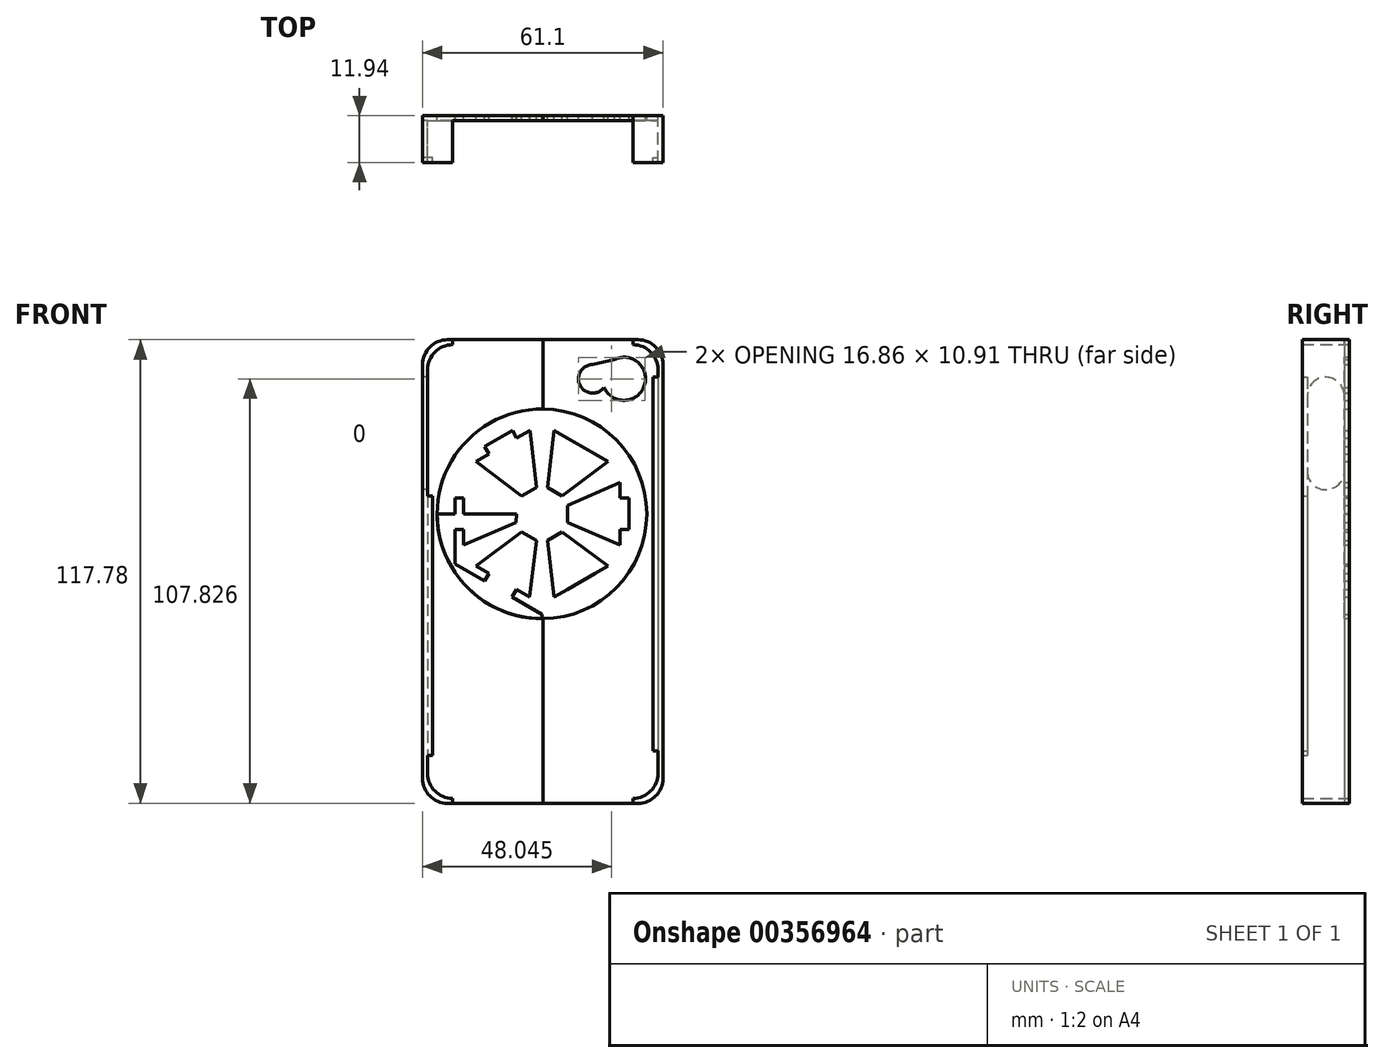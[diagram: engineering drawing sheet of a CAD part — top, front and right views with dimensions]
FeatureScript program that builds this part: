
annotation { "Feature Type Name" : "Feature", "Feature Type Description" : "" }
export const myFeature = defineFeature(function(context is Context, id is Id, definition is map)
    precondition{}
    {
        {
            var Q0;
            Q0=qCreatedBy(makeId("Front.planeOp"),FACE);
            var sketch = newSketch(context, id + "F0", { "sketchPlane" : qUnion([Q0])});
            skLineSegment(sketch, "E0.left", {"start": v(-75.12, 56.4) * mm, "end": v(-75.12, -46.14) * mm});
            skLineSegment(sketch, "E0.right", {"start": v(-16.58, 56.4) * mm, "end": v(-16.58, -46.14) * mm});
            skPoint(sketch, "E1.visualSharp", {"position": v(-16.58, 62.75) * mm});
            skArc(sketch, "E1.filletArc", {"start": v(-16.58, 56.4) * mm, "mid": v(-18.43, 60.88) * mm, "end": v(-22.9, 62.75) * mm});
            skPoint(sketch, "E2.visualSharp", {"position": v(-75.12, 62.75) * mm});
            skArc(sketch, "E2.filletArc", {"start": v(-68.77, 62.75) * mm, "mid": v(-73.26, 60.89) * mm, "end": v(-75.12, 56.4) * mm});
            skPoint(sketch, "E3.visualSharp", {"position": v(-75.12, -52.5) * mm});
            skArc(sketch, "E3.filletArc", {"start": v(-75.12, -46.14) * mm, "mid": v(-73.26, -50.63) * mm, "end": v(-68.77, -52.5) * mm});
            skPoint(sketch, "E4.visualSharp", {"position": v(-16.58, -52.5) * mm});
            skArc(sketch, "E4.filletArc", {"start": v(-22.93, -52.5) * mm, "mid": v(-18.44, -50.63) * mm, "end": v(-16.58, -46.14) * mm});
            skLineSegment(sketch, "E5.bottom", {"start": v(-70.04, 64.02) * mm, "end": v(-68.77, 64.02) * mm});
            skLineSegment(sketch, "E5.top", {"start": v(-70.04, -53.76) * mm, "end": v(-68.77, -53.76) * mm});
            skLineSegment(sketch, "E5.left", {"start": v(-76.4, 57.67) * mm, "end": v(-76.4, -47.41) * mm});
            skLineSegment(sketch, "E5.right", {"start": v(-15.3, 57.67) * mm, "end": v(-15.3, -47.41) * mm});
            skPoint(sketch, "E6.visualSharp", {"position": v(-15.3, 64.02) * mm});
            skArc(sketch, "E6.filletArc", {"start": v(-15.3, 57.67) * mm, "mid": v(-17.17, 62.16) * mm, "end": v(-21.66, 64.02) * mm});
            skPoint(sketch, "E7.visualSharp", {"position": v(-76.4, 64.02) * mm});
            skArc(sketch, "E7.filletArc", {"start": v(-70.04, 64.02) * mm, "mid": v(-74.53, 62.16) * mm, "end": v(-76.4, 57.67) * mm});
            skPoint(sketch, "E8.visualSharp", {"position": v(-76.4, -53.76) * mm});
            skArc(sketch, "E8.filletArc", {"start": v(-76.4, -47.41) * mm, "mid": v(-74.53, -51.9) * mm, "end": v(-70.04, -53.76) * mm});
            skPoint(sketch, "E9.visualSharp", {"position": v(-15.3, -53.76) * mm});
            skArc(sketch, "E9.filletArc", {"start": v(-21.66, -53.76) * mm, "mid": v(-17.17, -51.9) * mm, "end": v(-15.3, -47.41) * mm});
            skLineSegment(sketch, "E10", {"start": v(-68.77, -52.5) * mm, "end": v(-68.77, -53.76) * mm});
            skLineSegment(sketch, "E11", {"start": v(-22.93, -52.5) * mm, "end": v(-22.93, -53.76) * mm});
            skLineSegment(sketch, "E12.trimOffspring", {"start": v(-22.93, -53.76) * mm, "end": v(-21.66, -53.76) * mm});
            skLineSegment(sketch, "E13", {"start": v(-68.77, 62.75) * mm, "end": v(-68.77, 64.02) * mm});
            skLineSegment(sketch, "E14", {"start": v(-22.9, 62.75) * mm, "end": v(-22.9, 64.02) * mm});
            skLineSegment(sketch, "E15.trimOffspring", {"start": v(-22.9, 64.02) * mm, "end": v(-21.66, 64.02) * mm});
            skLineSegment(sketch, "E16", {"start": v(-68.77, 64.02) * mm, "end": v(-22.9, 64.02) * mm});
            skLineSegment(sketch, "E17", {"start": v(-68.77, -53.76) * mm, "end": v(-22.93, -53.76) * mm});
            skCircle(sketch, "E18", {"center": v(-25.24, 54.09) * mm, "radius": 5.48 * mm});
            skCircle(sketch, "E19", {"center": v(-33.16, 54.09) * mm, "radius": 3.63 * mm});
            skLineSegment(sketch, "E20", {"start": v(-25.24, 59.57) * mm, "end": v(-33.16, 57.72) * mm});
            skLineSegment(sketch, "E21", {"start": v(-26.52, 48.75) * mm, "end": v(-34.01, 50.56) * mm});
            skLineSegment(sketch, "E22", {"start": v(-45.84, 64.02) * mm, "end": v(-45.84, -53.76) * mm});
            skCircle(sketch, "E23", {"center": v(-46.06, 19.78) * mm, "radius": 26.63 * mm});
            skLineSegment(sketch, "E24", {"start": v(-46.06, 46.4) * mm, "end": v(-46.06, -6.85) * mm});
            skLineSegment(sketch, "E25.5", {"start": v(-46.06, 45.29) * mm, "end": v(-23.97, 32.53) * mm});
            skPoint(sketch, "E25.0.midPoint", {"position": v(-23.97, 19.78) * mm});
            skPoint(sketch, "E26.0.midPoint", {"position": v(-36.14, 37) * mm});
            skPoint(sketch, "E27.0.midPoint", {"position": v(-39.54, 19.78) * mm});
            skLineSegment(sketch, "E28", {"start": v(-44.67, 26.5) * mm, "end": v(-42.99, 40.94) * mm});
            skLineSegment(sketch, "E29", {"start": v(-38.53, 40.94) * mm, "end": v(-39.64, 39.01) * mm});
            skLineSegment(sketch, "E30", {"start": v(-42.99, 40.94) * mm, "end": v(-46.08, 42.72) * mm});
            skLineSegment(sketch, "E31", {"start": v(-40.93, 24.35) * mm, "end": v(-29.3, 33.05) * mm});
            skLineSegment(sketch, "E32", {"start": v(-32.64, 34.98) * mm, "end": v(-31.53, 36.9) * mm});
            skLineSegment(sketch, "E33", {"start": v(-26.2, 27.7) * mm, "end": v(-39.54, 21.94) * mm});
            skLineSegment(sketch, "E34", {"start": v(-26.2, 23.84) * mm, "end": v(-23.97, 23.84) * mm});
            skLineSegment(sketch, "E35", {"start": v(-46.06, 19.78) * mm, "end": v(-19.44, 19.8) * mm});
            skLineSegment(sketch, "E36", {"start": v(-23.97, 32.53) * mm, "end": v(-23.97, 19.78) * mm});
            skLineSegment(sketch, "E37", {"start": v(-26.2, 31.27) * mm, "end": v(-29.3, 33.05) * mm});
            skLineSegment(sketch, "E38", {"start": v(-29.3, 33.05) * mm, "end": v(-32.64, 34.98) * mm});
            skLineSegment(sketch, "E39", {"start": v(-32.64, 34.98) * mm, "end": v(-39.64, 39.01) * mm});
            skLineSegment(sketch, "E40", {"start": v(-39.64, 39.01) * mm, "end": v(-42.99, 40.94) * mm});
            skLineSegment(sketch, "E41", {"start": v(-26.2, 31.27) * mm, "end": v(-26.2, 27.7) * mm});
            skLineSegment(sketch, "E42", {"start": v(-26.2, 27.7) * mm, "end": v(-26.2, 23.84) * mm});
            skLineSegment(sketch, "E43", {"start": v(-26.2, 23.84) * mm, "end": v(-26.2, 19.8) * mm});
            skPoint(sketch, "E44", {"position": v(-46.06, 27.3) * mm});
            skLineSegment(sketch, "E45", {"start": v(-46.06, 27.3) * mm, "end": v(-44.67, 26.5) * mm});
            skLineSegment(sketch, "E46", {"start": v(-44.67, 26.5) * mm, "end": v(-40.93, 24.35) * mm});
            skLineSegment(sketch, "E47", {"start": v(-40.93, 24.35) * mm, "end": v(-39.54, 23.54) * mm});
            skLineSegment(sketch, "E48", {"start": v(-39.54, 23.54) * mm, "end": v(-39.54, 21.94) * mm});
            skLineSegment(sketch, "E49", {"start": v(-39.54, 21.94) * mm, "end": v(-39.54, 19.78) * mm});
            skLineSegment(sketch, "E50.MirrorCS", {"start": v(-46.02, -5.73) * mm, "end": v(-23.95, 7.06) * mm});
            skLineSegment(sketch, "E51.MirrorCS", {"start": v(-23.95, 7.06) * mm, "end": v(-23.97, 19.81) * mm});
            skLineSegment(sketch, "E52.MirrorCS", {"start": v(-42.95, -1.38) * mm, "end": v(-46.05, -3.16) * mm});
            skLineSegment(sketch, "E53.MirrorCS", {"start": v(-39.61, 0.56) * mm, "end": v(-42.95, -1.38) * mm});
            skLineSegment(sketch, "E54.MirrorCS", {"start": v(-38.5, -1.37) * mm, "end": v(-39.61, 0.56) * mm});
            skLineSegment(sketch, "E55.MirrorCS", {"start": v(-32.62, 4.6) * mm, "end": v(-39.61, 0.56) * mm});
            skLineSegment(sketch, "E56.MirrorCS", {"start": v(-32.62, 4.6) * mm, "end": v(-31.5, 2.68) * mm});
            skLineSegment(sketch, "E57.MirrorCS", {"start": v(-29.28, 6.54) * mm, "end": v(-32.62, 4.6) * mm});
            skLineSegment(sketch, "E58.MirrorCS", {"start": v(-26.19, 8.32) * mm, "end": v(-29.28, 6.54) * mm});
            skLineSegment(sketch, "E59.MirrorCS", {"start": v(-26.19, 8.32) * mm, "end": v(-26.19, 11.9) * mm});
            skLineSegment(sketch, "E60.MirrorCS", {"start": v(-26.19, 11.9) * mm, "end": v(-26.2, 15.76) * mm});
            skLineSegment(sketch, "E61.MirrorCS", {"start": v(-26.2, 15.76) * mm, "end": v(-26.2, 19.8) * mm});
            skLineSegment(sketch, "E62.MirrorCS", {"start": v(-26.19, 11.9) * mm, "end": v(-39.54, 17.63) * mm});
            skLineSegment(sketch, "E63.MirrorCS", {"start": v(-40.93, 15.22) * mm, "end": v(-29.28, 6.54) * mm});
            skLineSegment(sketch, "E64.MirrorCS", {"start": v(-44.66, 13.06) * mm, "end": v(-42.95, -1.38) * mm});
            skLineSegment(sketch, "E65.MirrorCS", {"start": v(-44.66, 13.06) * mm, "end": v(-40.93, 15.22) * mm});
            skPoint(sketch, "E66.MirrorP", {"position": v(-46.05, 12.25) * mm});
            skLineSegment(sketch, "E67.MirrorCS", {"start": v(-46.05, 12.25) * mm, "end": v(-44.66, 13.06) * mm});
            skLineSegment(sketch, "E68.MirrorCS", {"start": v(-40.93, 15.22) * mm, "end": v(-39.54, 16.03) * mm});
            skLineSegment(sketch, "E69.MirrorCS", {"start": v(-39.54, 16.03) * mm, "end": v(-39.54, 17.63) * mm});
            skLineSegment(sketch, "E70.MirrorCS", {"start": v(-39.54, 17.63) * mm, "end": v(-39.54, 19.79) * mm});
            skLineSegment(sketch, "E71.MirrorCS", {"start": v(-52.59, 16.03) * mm, "end": v(-52.59, 17.63) * mm});
            skLineSegment(sketch, "E72.MirrorCS", {"start": v(-51.2, 15.22) * mm, "end": v(-52.59, 16.03) * mm});
            skLineSegment(sketch, "E73.MirrorCS", {"start": v(-52.58, 21.94) * mm, "end": v(-52.58, 19.78) * mm});
            skLineSegment(sketch, "E74.MirrorCS", {"start": v(-51.2, 24.35) * mm, "end": v(-52.58, 23.54) * mm});
            skLineSegment(sketch, "E75.MirrorCS", {"start": v(-52.59, 17.63) * mm, "end": v(-52.58, 19.79) * mm});
            skLineSegment(sketch, "E76.MirrorCS", {"start": v(-52.58, 23.54) * mm, "end": v(-52.58, 21.94) * mm});
            skLineSegment(sketch, "E77.MirrorCS", {"start": v(-65.93, 23.84) * mm, "end": v(-68.16, 23.84) * mm});
            skLineSegment(sketch, "E78.MirrorCS", {"start": v(-53.63, -1.37) * mm, "end": v(-52.52, 0.56) * mm});
            skLineSegment(sketch, "E79.MirrorCS", {"start": v(-59.49, 34.98) * mm, "end": v(-60.6, 36.9) * mm});
            skLineSegment(sketch, "E80.MirrorCS", {"start": v(-59.5, 4.6) * mm, "end": v(-60.62, 2.68) * mm});
            skLineSegment(sketch, "E81.MirrorCS", {"start": v(-53.6, 40.94) * mm, "end": v(-52.48, 39.01) * mm});
            skLineSegment(sketch, "E82.MirrorCS", {"start": v(-65.94, 11.9) * mm, "end": v(-65.94, 15.76) * mm});
            skPoint(sketch, "E83.MirrorP", {"position": v(-52.58, 19.78) * mm});
            skLineSegment(sketch, "E84.MirrorCS", {"start": v(-65.93, 23.84) * mm, "end": v(-65.93, 19.8) * mm});
            skLineSegment(sketch, "E85.MirrorCS", {"start": v(-49.17, -1.38) * mm, "end": v(-46.08, -3.16) * mm});
            skLineSegment(sketch, "E86.MirrorCS", {"start": v(-62.85, 6.54) * mm, "end": v(-59.5, 4.6) * mm});
            skLineSegment(sketch, "E87.MirrorCS", {"start": v(-47.47, 13.06) * mm, "end": v(-49.17, -1.38) * mm});
            skLineSegment(sketch, "E88.MirrorCS", {"start": v(-68.18, 7.06) * mm, "end": v(-68.15, 19.81) * mm});
            skLineSegment(sketch, "E89.MirrorCS", {"start": v(-62.83, 33.05) * mm, "end": v(-59.49, 34.98) * mm});
            skLineSegment(sketch, "E90.MirrorCS", {"start": v(-65.94, 15.76) * mm, "end": v(-65.93, 19.8) * mm});
            skLineSegment(sketch, "E91.MirrorCS", {"start": v(-59.49, 34.98) * mm, "end": v(-52.48, 39.01) * mm});
            skLineSegment(sketch, "E92.MirrorCS", {"start": v(-52.48, 39.01) * mm, "end": v(-49.14, 40.94) * mm});
            skLineSegment(sketch, "E93.MirrorCS", {"start": v(-65.94, 8.32) * mm, "end": v(-65.94, 11.9) * mm});
            skPoint(sketch, "E94.MirrorP", {"position": v(-55.98, 37) * mm});
            skLineSegment(sketch, "E95.MirrorCS", {"start": v(-65.93, 27.7) * mm, "end": v(-65.93, 23.84) * mm});
            skLineSegment(sketch, "E96.MirrorCS", {"start": v(-65.93, 27.7) * mm, "end": v(-52.58, 21.94) * mm});
            skLineSegment(sketch, "E97.MirrorCS", {"start": v(-46.06, 19.78) * mm, "end": v(-72.69, 19.8) * mm});
            skLineSegment(sketch, "E98.MirrorCS", {"start": v(-51.2, 24.35) * mm, "end": v(-62.83, 33.05) * mm});
            skPoint(sketch, "E99.MirrorP", {"position": v(-46.08, 12.25) * mm});
            skLineSegment(sketch, "E100.MirrorCS", {"start": v(-51.2, 15.22) * mm, "end": v(-62.85, 6.54) * mm});
            skLineSegment(sketch, "E101.MirrorCS", {"start": v(-47.47, 13.06) * mm, "end": v(-51.2, 15.22) * mm});
            skLineSegment(sketch, "E102.MirrorCS", {"start": v(-47.45, 26.5) * mm, "end": v(-49.14, 40.94) * mm});
            skLineSegment(sketch, "E103.MirrorCS", {"start": v(-65.94, 8.32) * mm, "end": v(-62.85, 6.54) * mm});
            skLineSegment(sketch, "E104.MirrorCS", {"start": v(-46.06, 45.29) * mm, "end": v(-68.15, 32.53) * mm});
            skLineSegment(sketch, "E105.MirrorCS", {"start": v(-68.15, 32.53) * mm, "end": v(-68.15, 19.78) * mm});
            skLineSegment(sketch, "E106.MirrorCS", {"start": v(-52.52, 0.56) * mm, "end": v(-49.17, -1.38) * mm});
            skLineSegment(sketch, "E107.MirrorCS", {"start": v(-49.14, 40.94) * mm, "end": v(-46.05, 42.72) * mm});
            skPoint(sketch, "E108.MirrorP", {"position": v(-68.15, 19.78) * mm});
            skLineSegment(sketch, "E109.MirrorCS", {"start": v(-65.92, 31.27) * mm, "end": v(-65.93, 27.7) * mm});
            skLineSegment(sketch, "E110.MirrorCS", {"start": v(-47.45, 26.5) * mm, "end": v(-51.2, 24.35) * mm});
            skLineSegment(sketch, "E111.MirrorCS", {"start": v(-59.5, 4.6) * mm, "end": v(-52.52, 0.56) * mm});
            skLineSegment(sketch, "E112.MirrorCS", {"start": v(-65.94, 11.9) * mm, "end": v(-52.59, 17.63) * mm});
            skLineSegment(sketch, "E113.MirrorCS", {"start": v(-46.1, -5.73) * mm, "end": v(-68.18, 7.06) * mm});
            skLineSegment(sketch, "E114.MirrorCS", {"start": v(-65.92, 31.27) * mm, "end": v(-62.83, 33.05) * mm});
            skLineSegment(sketch, "E115.MirrorCS", {"start": v(-46.06, 27.3) * mm, "end": v(-47.45, 26.5) * mm});
            skLineSegment(sketch, "E116.MirrorCS", {"start": v(-46.08, 12.25) * mm, "end": v(-47.47, 13.06) * mm});
            skLineSegment(sketch, "E117.MirrorCS", {"start": v(-26.2, 15.76) * mm, "end": v(-23.96, 15.76) * mm});
            skLineSegment(sketch, "E118.MirrorCS", {"start": v(-65.94, 15.76) * mm, "end": v(-68.16, 15.76) * mm});
            skLineSegment(sketch, "E119", {"start": v(-46.1, -5.73) * mm, "end": v(-46.06, -5.75) * mm});
            skLineSegment(sketch, "E120", {"start": v(-46.06, -5.75) * mm, "end": v(-46.02, -5.73) * mm});
            skLineSegment(sketch, "E121", {"start": v(-46.08, 12.25) * mm, "end": v(-46.06, 12.24) * mm});
            skLineSegment(sketch, "E122", {"start": v(-46.06, 12.24) * mm, "end": v(-46.05, 12.25) * mm});
            skSolve(sketch);
        }
        {
            var Q0;
            Q0=makeQuery(id+"F0.imprint","IMPRINT",FACE,{"disambiguationData":[TD([[makeQuery(id+"F0.imprint","IMPRINT",EDGE,{"derivedFrom":sQuery(id+"F0.wireOp",EDGE,"E0.left")}),1.0]])]});
            extrude(context, id + "F1", {"entities" : qUnion([Q0]), "depth" : 1.27 * mm});
        }
        {
            var Q0;
            Q0=makeQuery(id+"F0.imprint","IMPRINT",FACE,{"disambiguationData":[TD([[makeQuery(id+"F0.imprint","IMPRINT",EDGE,{"derivedFrom":sQuery(id+"F0.wireOp",EDGE,"E0.left")}),-1.0]])]});
            var Q1;
            Q1=makeQuery(id+"F0.imprint","IMPRINT",FACE,{"disambiguationData":[TD([[makeQuery(id+"F0.imprint","IMPRINT",EDGE,{"derivedFrom":sQuery(id+"F0.wireOp",EDGE,"E0.right")}),1.0]])]});
            extrude(context, id + "F2", {"entities" : qUnion([Q0, Q1]), "operationType" : NewBodyOperationType.ADD, "depth" : 11.94 * mm});
        }
        {
            var Q0;
            Q0=makeQuery(id+"F2.opExtrude","SWEPT_FACE",FACE,{"disambiguationData":[OSD([sQuery(id+"F0.wireOp",EDGE,"E5.left")])]});
            var sketch = newSketch(context, id + "F3", { "sketchPlane" : qUnion([Q0])});
            skCircle(sketch, "E123", {"center": v(5.97, 49.8) * mm, "radius": 4.7 * mm});
            skCircle(sketch, "E124", {"center": v(5.97, 30.62) * mm, "radius": 4.7 * mm});
            skLineSegment(sketch, "E125", {"start": v(1.27, 49.8) * mm, "end": v(1.27, 30.62) * mm});
            skLineSegment(sketch, "E126", {"start": v(10.67, 30.62) * mm, "end": v(10.67, 49.8) * mm});
            skSolve(sketch);
        }
        {
            var Q0;
            {var subQ0=sQuery(id+"F3.wireOp",EDGE,"E125");Q0=makeQuery(id+"F3.imprint","IMPRINT",FACE,{"disambiguationData":[TD([[makeQuery(id+"F3.imprint","IMPRINT",EDGE,{"derivedFrom":subQ0}),1.0]])]});}
            var Q1;
            {var subQ0=sQuery(id+"F3.wireOp",EDGE,"E123");var subQ1=makeQuery(id+"F3.imprint","INTERSECT",VERTEX,{"derivedFrom":[subQ0,sQuery(id+"F3.wireOp",EDGE,"E125")]});Q1=makeQuery(id+"F3.imprint","IMPRINT",FACE,{"disambiguationData":[TD([[makeQuery(id+"F3.imprint","IMPRINT",EDGE,{"disambiguationData":[TD([[subQ1,1.0]])],"derivedFrom":subQ0}),1.0]])]});}
            var Q2;
            {var subQ0=sQuery(id+"F3.wireOp",EDGE,"E124");var subQ1=makeQuery(id+"F3.imprint","INTERSECT",VERTEX,{"derivedFrom":[subQ0,sQuery(id+"F3.wireOp",EDGE,"E125")]});Q2=makeQuery(id+"F3.imprint","IMPRINT",FACE,{"disambiguationData":[TD([[makeQuery(id+"F3.imprint","IMPRINT",EDGE,{"disambiguationData":[TD([[subQ1,1.0]])],"derivedFrom":subQ0}),1.0]])]});}
            extrude(context, id + "F4", {"entities" : qUnion([Q0, Q1, Q2]), "operationType" : NewBodyOperationType.REMOVE, "oppositeDirection" : true, "depth" : 25.4 * mm});
        }
        {
            var Q0;
            Q0=makeQuery(id+"F0.imprint","IMPRINT",FACE,{"disambiguationData":[TD([[makeQuery(id+"F0.imprint","IMPRINT",EDGE,{"derivedFrom":sQuery(id+"F0.wireOp",EDGE,"E0.right")}),-1.0]])]});
            extrude(context, id + "F5", {"entities" : qUnion([Q0]), "depth" : 1.27 * mm});
        }
        {
            var Q0;
            {var subQ7=sQuery(id+"F0.wireOp",EDGE,"E105.MirrorCS");var subQ9=makeQuery(id+"F0.imprint","IMPRINT",VERTEX,{"derivedFrom":subQ7});Q0=makeQuery(id+"F0.imprint","IMPRINT",FACE,{"disambiguationData":[TD([[makeQuery(id+"F0.imprint","IMPRINT",EDGE,{"disambiguationData":[TD([[subQ9,1.0]])],"derivedFrom":subQ7}),-1.0]])]});}
            var Q1;
            {var subQ11=sQuery(id+"F0.wireOp",EDGE,"E119");Q1=makeQuery(id+"F0.imprint","IMPRINT",FACE,{"disambiguationData":[TD([[makeQuery(id+"F0.imprint","IMPRINT",EDGE,{"derivedFrom":subQ11}),-1.0]])]});}
            var Q2;
            {var subQ8=sQuery(id+"F0.wireOp",EDGE,"E51.MirrorCS");var subQ10=makeQuery(id+"F0.imprint","IMPRINT",VERTEX,{"derivedFrom":subQ8});Q2=makeQuery(id+"F0.imprint","IMPRINT",FACE,{"disambiguationData":[TD([[makeQuery(id+"F0.imprint","IMPRINT",EDGE,{"disambiguationData":[TD([[subQ10,1.0]])],"derivedFrom":subQ8}),-1.0]])]});}
            var Q3;
            {var subQ5=sQuery(id+"F0.wireOp",EDGE,"E22");var subQ7=sQuery(id+"F0.wireOp",EDGE,"E23");var subQ8=makeQuery(id+"F0.imprint","INTERSECT",VERTEX,{"disambiguationData":[OD(0.0)],"derivedFrom":[subQ5,subQ7]});Q3=makeQuery(id+"F0.imprint","IMPRINT",FACE,{"disambiguationData":[TD([[makeQuery(id+"F0.imprint","IMPRINT",EDGE,{"disambiguationData":[TD([[subQ8,-1.0]])],"derivedFrom":subQ5}),1.0]])]});}
            var Q4;
            Q4=makeQuery(id+"F0.imprint","IMPRINT",FACE,{"disambiguationData":[TD([[makeQuery(id+"F0.imprint","IMPRINT",EDGE,{"derivedFrom":sQuery(id+"F0.wireOp",EDGE,"E28")}),-1.0]])]});
            var Q5;
            {var subQ0=sQuery(id+"F0.wireOp",EDGE,"E29");Q5=makeQuery(id+"F0.imprint","IMPRINT",FACE,{"disambiguationData":[TD([[makeQuery(id+"F0.imprint","IMPRINT",EDGE,{"derivedFrom":subQ0}),1.0]])]});}
            var Q6;
            Q6=makeQuery(id+"F0.imprint","IMPRINT",FACE,{"disambiguationData":[TD([[makeQuery(id+"F0.imprint","IMPRINT",EDGE,{"derivedFrom":sQuery(id+"F0.wireOp",EDGE,"E89.MirrorCS")}),-1.0]])]});
            var Q7;
            {var subQ0=sQuery(id+"F0.wireOp",EDGE,"E79.MirrorCS");Q7=makeQuery(id+"F0.imprint","IMPRINT",FACE,{"disambiguationData":[TD([[makeQuery(id+"F0.imprint","IMPRINT",EDGE,{"derivedFrom":subQ0}),-1.0]])]});}
            var Q8;
            {var subQ2=sQuery(id+"F0.wireOp",EDGE,"E73.MirrorCS");Q8=makeQuery(id+"F0.imprint","IMPRINT",FACE,{"disambiguationData":[TD([[makeQuery(id+"F0.imprint","IMPRINT",EDGE,{"derivedFrom":subQ2}),-1.0]])]});}
            var Q9;
            Q9=makeQuery(id+"F0.imprint","IMPRINT",FACE,{"disambiguationData":[TD([[makeQuery(id+"F0.imprint","IMPRINT",EDGE,{"derivedFrom":sQuery(id+"F0.wireOp",EDGE,"E82.MirrorCS")}),-1.0]])]});
            var Q10;
            {var subQ5=sQuery(id+"F0.wireOp",EDGE,"E90.MirrorCS");Q10=makeQuery(id+"F0.imprint","IMPRINT",FACE,{"disambiguationData":[TD([[makeQuery(id+"F0.imprint","IMPRINT",EDGE,{"derivedFrom":subQ5}),1.0]])]});}
            var Q11;
            {var subQ5=sQuery(id+"F0.wireOp",EDGE,"E84.MirrorCS");Q11=makeQuery(id+"F0.imprint","IMPRINT",FACE,{"disambiguationData":[TD([[makeQuery(id+"F0.imprint","IMPRINT",EDGE,{"derivedFrom":subQ5}),-1.0]])]});}
            var Q12;
            Q12=makeQuery(id+"F0.imprint","IMPRINT",FACE,{"disambiguationData":[TD([[makeQuery(id+"F0.imprint","IMPRINT",EDGE,{"derivedFrom":sQuery(id+"F0.wireOp",EDGE,"E86.MirrorCS")}),1.0]])]});
            var Q13;
            {var subQ0=sQuery(id+"F0.wireOp",EDGE,"E78.MirrorCS");Q13=makeQuery(id+"F0.imprint","IMPRINT",FACE,{"disambiguationData":[TD([[makeQuery(id+"F0.imprint","IMPRINT",EDGE,{"derivedFrom":subQ0}),1.0]])]});}
            var Q14;
            Q14=makeQuery(id+"F0.imprint","IMPRINT",FACE,{"disambiguationData":[TD([[makeQuery(id+"F0.imprint","IMPRINT",EDGE,{"derivedFrom":sQuery(id+"F0.wireOp",EDGE,"E53.MirrorCS")}),-1.0]])]});
            var Q15;
            {var subQ0=sQuery(id+"F0.wireOp",EDGE,"E54.MirrorCS");Q15=makeQuery(id+"F0.imprint","IMPRINT",FACE,{"disambiguationData":[TD([[makeQuery(id+"F0.imprint","IMPRINT",EDGE,{"derivedFrom":subQ0}),-1.0]])]});}
            var Q16;
            Q16=makeQuery(id+"F0.imprint","IMPRINT",FACE,{"disambiguationData":[TD([[makeQuery(id+"F0.imprint","IMPRINT",EDGE,{"derivedFrom":sQuery(id+"F0.wireOp",EDGE,"E60.MirrorCS")}),1.0]])]});
            var Q17;
            Q17=makeQuery(id+"F0.imprint","IMPRINT",FACE,{"disambiguationData":[TD([[makeQuery(id+"F0.imprint","IMPRINT",EDGE,{"derivedFrom":sQuery(id+"F0.wireOp",EDGE,"E33")}),1.0]])]});
            var Q18;
            {var subQ5=sQuery(id+"F0.wireOp",EDGE,"E43");Q18=makeQuery(id+"F0.imprint","IMPRINT",FACE,{"disambiguationData":[TD([[makeQuery(id+"F0.imprint","IMPRINT",EDGE,{"derivedFrom":subQ5}),1.0]])]});}
            var Q19;
            {var subQ0=sQuery(id+"F0.wireOp",EDGE,"E61.MirrorCS");Q19=makeQuery(id+"F0.imprint","IMPRINT",FACE,{"disambiguationData":[TD([[makeQuery(id+"F0.imprint","IMPRINT",EDGE,{"derivedFrom":subQ0}),-1.0]])]});}
            extrude(context, id + "F6", {"entities" : qUnion([Q0, Q1, Q2, Q3, Q4, Q5, Q6, Q7, Q8, Q9, Q10, Q11, Q12, Q13, Q14, Q15, Q16, Q17, Q18, Q19]), "depth" : 1.27 * mm});
        }
        {
            var Q0;
            Q0=makeQuery(id+"F2.opExtrude","SWEPT_FACE",FACE,{"disambiguationData":[OSD([sQuery(id+"F0.wireOp",EDGE,"E0.left")])]});
            var sketch = newSketch(context, id + "F7", { "sketchPlane" : qUnion([Q0])});
            skLineSegment(sketch, "E127.bottom", {"start": v(-11.94, 24.38) * mm, "end": v(-10.67, 24.38) * mm});
            skLineSegment(sketch, "E127.top", {"start": v(-11.94, -41.62) * mm, "end": v(-10.67, -41.62) * mm});
            skLineSegment(sketch, "E127.left", {"start": v(-11.94, 24.38) * mm, "end": v(-11.94, -41.62) * mm});
            skLineSegment(sketch, "E127.right", {"start": v(-10.67, 24.38) * mm, "end": v(-10.67, -41.62) * mm});
            skSolve(sketch);
        }
        {
            var Q0;
            Q0=makeQuery(id+"F7.imprint","IMPRINT",FACE,{"disambiguationData":[TD([[makeQuery(id+"F7.imprint","IMPRINT",EDGE,{"derivedFrom":sQuery(id+"F7.wireOp",EDGE,"E127.bottom")}),-1.0]])]});
            extrude(context, id + "F8", {"entities" : qUnion([Q0]), "operationType" : NewBodyOperationType.ADD, "depth" : 1.27 * mm});
        }
        {
            var Q0;
            Q0=makeQuery(id+"F2.opExtrude","SWEPT_FACE",FACE,{"disambiguationData":[OSD([sQuery(id+"F0.wireOp",EDGE,"E0.right")])]});
            var sketch = newSketch(context, id + "F9", { "sketchPlane" : qUnion([Q0])});
            skLineSegment(sketch, "E128.bottom", {"start": v(11.94, 54.52) * mm, "end": v(10.67, 54.52) * mm});
            skLineSegment(sketch, "E128.top", {"start": v(11.94, -40.48) * mm, "end": v(10.67, -40.48) * mm});
            skLineSegment(sketch, "E128.left", {"start": v(11.94, 54.52) * mm, "end": v(11.94, -40.48) * mm});
            skLineSegment(sketch, "E128.right", {"start": v(10.67, 54.52) * mm, "end": v(10.67, -40.48) * mm});
            skSolve(sketch);
        }
        {
            var Q0;
            Q0=makeQuery(id+"F9.imprint","IMPRINT",FACE,{"disambiguationData":[TD([[makeQuery(id+"F9.imprint","IMPRINT",EDGE,{"derivedFrom":sQuery(id+"F9.wireOp",EDGE,"E128.bottom")}),1.0]])]});
            extrude(context, id + "F10", {"entities" : qUnion([Q0]), "operationType" : NewBodyOperationType.ADD, "depth" : 1.27 * mm});
        }
    });
